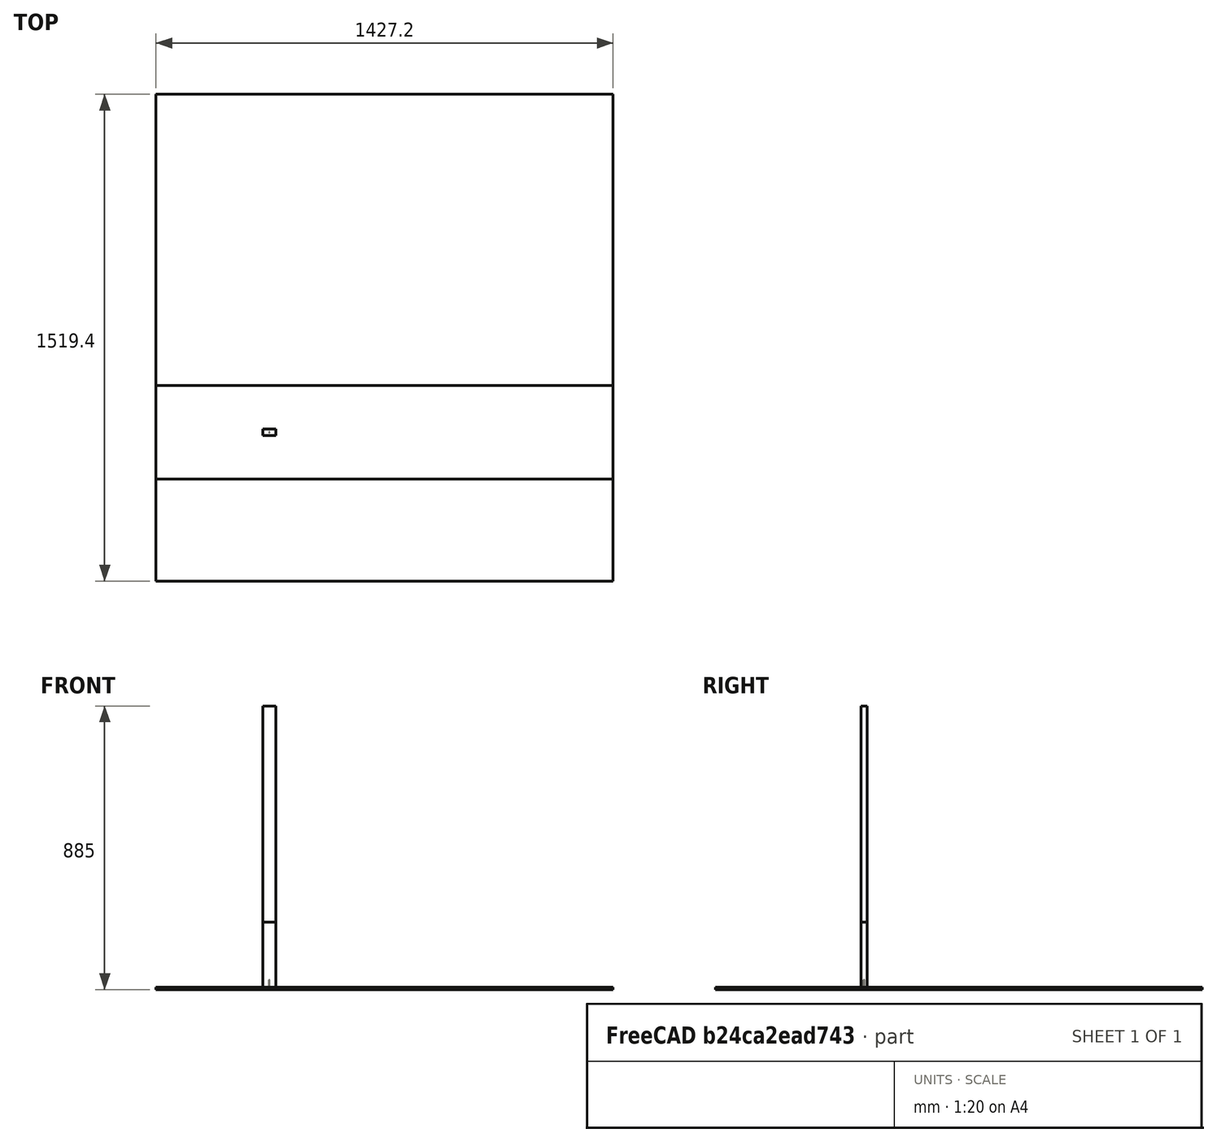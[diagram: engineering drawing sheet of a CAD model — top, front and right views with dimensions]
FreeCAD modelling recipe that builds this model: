
FCSTD DOCUMENT  (FreeCAD 0.22R37100 (Git))
Label: composit_stand10_transport
License: All rights reserved
LicenseURL: http://en.wikipedia.org/wiki/All_rights_reserved
objects: PartDesign::CoordinateSystem×13, App::FeaturePython×13, App::Link×12, Part::FeaturePython×10, App::DocumentObjectGroup×9, Sketcher::SketchObject×8, Path::FeaturePython×7, PartDesign::Pad×5, PartDesign::Body×5, PartDesign::Pocket×3, Measure::MeasureLength×2, Assembly::JointGroup×1, Assembly::AssemblyObject×1
note: 55 computed .brp shape members not serialized (recipe doc carries the construction recipe); baked Part::Feature solids carry a one-line shape summary decoded from their .brp

FEATURE [Sketcher::SketchObject] Sketch  label="front_Sketch"
  AttachmentSupport = -> [XY_Plane]
  FullyConstrained = true
  MapMode = 5
  sketch-geometry (5):
    g0: LineSegment StartX=-355.5 StartY=-465.5 StartZ=0 EndX=355.5 EndY=-465.5 EndZ=0
    g1: LineSegment StartX=355.5 StartY=-465.5 StartZ=0 EndX=355.5 EndY=465.5 EndZ=0
    g2: LineSegment StartX=355.5 StartY=465.5 StartZ=0 EndX=-355.5 EndY=465.5 EndZ=0
    g3: LineSegment StartX=-355.5 StartY=465.5 StartZ=0 EndX=-355.5 EndY=-465.5 EndZ=0
    g4: GeomPoint X=0 Y=0 Z=0
  constraints (12):
    c: Coincident(g0,g1)
    c: Coincident(g1,g2)
    c: Coincident(g2,g3)
    c: Coincident(g3,g0)
    c: Horizontal(g0)
    c: Horizontal(g2)
    c: Vertical(g1)
    c: Vertical(g3)
    c: Symmetric(g2,g0,g4)
    c: Coincident(g4,g-1)
    c: DistanceX(g0,g1) = 711  'width'
    c: DistanceY(g0,g1) = 931  'height'
FEATURE [PartDesign::Pad] Pad
  Direction = (0,0,1)
  Length = 6
  Length2 = 10
  Profile = -> Sketch
  ReferenceAxis = -> Sketch [N_Axis]
  Suppressed = false
  Type = 0
FEATURE [Sketcher::SketchObject] Sketch001  label="bottom_Sketch"
  AttachmentSupport = -> [XY_Plane001]
  FullyConstrained = true
  MapMode = 5
  sketch-geometry (5):
    g0: LineSegment StartX=-355.5 StartY=-145 StartZ=0 EndX=355.5 EndY=-145 EndZ=0
    g1: LineSegment StartX=355.5 StartY=-145 StartZ=0 EndX=355.5 EndY=145 EndZ=0
    g2: LineSegment StartX=355.5 StartY=145 StartZ=0 EndX=-355.5 EndY=145 EndZ=0
    g3: LineSegment StartX=-355.5 StartY=145 StartZ=0 EndX=-355.5 EndY=-145 EndZ=0
    g4: GeomPoint X=0 Y=0 Z=0
  constraints (12):
    c: Coincident(g0,g1)
    c: Coincident(g1,g2)
    c: Coincident(g2,g3)
    c: Coincident(g3,g0)
    c: Horizontal(g0)
    c: Horizontal(g2)
    c: Vertical(g1)
    c: Vertical(g3)
    c: Symmetric(g2,g0,g4)
    c: Coincident(g4,g-1)
    c: DistanceX(g0,g1) = 711  'width'
    c: DistanceY(g0,g1) = 290  'length'
FEATURE [PartDesign::Pad] Pad001
  Direction = (0,0,1)
  Length = 6
  Length2 = 10
  Profile = -> Sketch001
  ReferenceAxis = -> Sketch001 [N_Axis]
  Suppressed = false
  Type = 0
FEATURE [Sketcher::SketchObject] Sketch002  label="side_Sketch"
  AttachmentSupport = -> [XY_Plane002]
  FullyConstrained = true
  MapMode = 5
  sketch-geometry (5):
    g0: LineSegment StartX=-145 StartY=-442.5 StartZ=0 EndX=145 EndY=-442.5 EndZ=0
    g1: LineSegment StartX=145 StartY=-442.5 StartZ=0 EndX=145 EndY=442.5 EndZ=0
    g2: LineSegment StartX=145 StartY=442.5 StartZ=0 EndX=-145 EndY=442.5 EndZ=0
    g3: LineSegment StartX=-145 StartY=442.5 StartZ=0 EndX=-145 EndY=-442.5 EndZ=0
    g4: GeomPoint X=0 Y=0 Z=0
  constraints (12):
    c: Coincident(g0,g1)
    c: Coincident(g1,g2)
    c: Coincident(g2,g3)
    c: Coincident(g3,g0)
    c: Horizontal(g0)
    c: Horizontal(g2)
    c: Vertical(g1)
    c: Vertical(g3)
    c: Symmetric(g2,g0,g4)
    c: Coincident(g4,g-1)
    c: DistanceX(g0,g1) = 290  'length'
    c: DistanceY(g0,g1) = 885  'height'
FEATURE [PartDesign::Pad] Pad002
  Direction = (0,0,1)
  Length = 6
  Length2 = 10
  Profile = -> Sketch002
  ReferenceAxis = -> Sketch002 [N_Axis]
  Suppressed = false
  Type = 0
FEATURE [Sketcher::SketchObject] Sketch003  label="bar_big_Sketch"
  AttachmentSupport = -> [XY_Plane003]
  FullyConstrained = true
  MapMode = 5
  sketch-geometry (5):
    g0: LineSegment StartX=-20 StartY=-10 StartZ=0 EndX=20 EndY=-10 EndZ=0
    g1: LineSegment StartX=20 StartY=-10 StartZ=0 EndX=20 EndY=10 EndZ=0
    g2: LineSegment StartX=20 StartY=10 StartZ=0 EndX=-20 EndY=10 EndZ=0
    g3: LineSegment StartX=-20 StartY=10 StartZ=0 EndX=-20 EndY=-10 EndZ=0
    g4: GeomPoint X=0 Y=0 Z=0
  constraints (12):
    c: Coincident(g0,g1)
    c: Coincident(g1,g2)
    c: Coincident(g2,g3)
    c: Coincident(g3,g0)
    c: Horizontal(g0)
    c: Horizontal(g2)
    c: Vertical(g1)
    c: Vertical(g3)
    c: Symmetric(g2,g0,g4)
    c: Coincident(g4,g-1)
    c: DistanceX(g0,g1) = 40
    c: DistanceY(g0,g1) = 20
FEATURE [PartDesign::Pad] Pad003
  Direction = (0,0,1)
  Length = 885
  Length2 = 10
  Profile = -> Sketch003
  ReferenceAxis = -> Sketch003 [N_Axis]
  Suppressed = false
  Type = 0
FEATURE [Sketcher::SketchObject] Sketch004  label="bar_small_Sketch"
  AttachmentSupport = -> [XY_Plane004]
  FullyConstrained = true
  MapMode = 5
  sketch-geometry (5):
    g0: LineSegment StartX=-20 StartY=-10 StartZ=0 EndX=20 EndY=-10 EndZ=0
    g1: LineSegment StartX=20 StartY=-10 StartZ=0 EndX=20 EndY=10 EndZ=0
    g2: LineSegment StartX=20 StartY=10 StartZ=0 EndX=-20 EndY=10 EndZ=0
    g3: LineSegment StartX=-20 StartY=10 StartZ=0 EndX=-20 EndY=-10 EndZ=0
    g4: GeomPoint X=0 Y=0 Z=0
  constraints (12):
    c: Coincident(g0,g1)
    c: Coincident(g1,g2)
    c: Coincident(g2,g3)
    c: Coincident(g3,g0)
    c: Horizontal(g0)
    c: Horizontal(g2)
    c: Vertical(g1)
    c: Vertical(g3)
    c: Symmetric(g2,g0,g4)
    c: Coincident(g4,g-1)
    c: DistanceX(g0,g1) = 40
    c: DistanceY(g0,g1) = 20
FEATURE [PartDesign::Pad] Pad004
  Direction = (0,0,1)
  Length = 210
  Length2 = 10
  Profile = -> Sketch004
  ReferenceAxis = -> Sketch004 [N_Axis]
  Suppressed = false
  Type = 0
FEATURE [PartDesign::CoordinateSystem] Local_CS  label="front_bottom_LCS"
  AttacherType = Attacher::AttachEngine3D
  AttachmentOffset = pos=(0,-445.5,0) rot=(0,0,1;0rad)
  AttachmentSupport = -> [XY_Plane]
  MapMode = 5
  Placement = pos=(0,-445.5,0) rot=(0,0,1;0rad)
  expr: .AttachmentOffset.Base.y = -<<front_Sketch>>.Constraints.height / 2 + 20 mm
FEATURE [PartDesign::CoordinateSystem] Local_CS001  label="bottom_front_LCS"
  AttacherType = Attacher::AttachEngine3D
  AttachmentOffset = pos=(0,-145,0) rot=(1,0,0;1.5708rad)
  AttachmentSupport = -> [XY_Plane001]
  MapMode = 5
  Placement = pos=(0,-145,0) rot=(1,0,0;1.5708rad)
  expr: .AttachmentOffset.Base.y = -<<bottom_Sketch>>.Constraints.length / 2
FEATURE [PartDesign::CoordinateSystem] Local_CS002  label="bottom_side_LCS"
  AttacherType = Attacher::AttachEngine3D
  AttachmentOffset = pos=(329.5,0,6) rot=(0.57735,0.57735,0.57735;2.0944rad)
  AttachmentSupport = -> [XY_Plane001]
  MapMode = 5
  Placement = pos=(329.5,0,6) rot=(0.57735,0.57735,0.57735;2.0944rad)
  expr: .AttachmentOffset.Base.x = <<bottom_Sketch>>.Constraints.width / 2 - 26 mm
FEATURE [App::FeaturePython] SetupSheet  # Path/CAM operation (typed FeaturePython)
  ClearanceHeightExpression = OpStockZMax+SetupSheet.ClearanceHeightOffset
  ClearanceHeightOffset = 5
  CoolantMode = 0
  CoolantModes = None | Flood | Mist
  FinalDepthExpression = OpFinalDepth
  HorizRapid = 0
  ProfileDirection = 1
  ProfileprocessCircles = true
  ProfileprocessHoles = true
  ProfileprocessPerimeter = true
  SafeHeightExpression = OpStockZMax+SetupSheet.SafeHeightOffset
  SafeHeightOffset = 3
  StartDepthExpression = OpStartDepth
  StepDownExpression = OpToolDiameter
  VertRapid = 0
FEATURE [Part::FeaturePython] ToolBit  label="3.175mm Endmill"  # Path/CAM toolbit (typed FeaturePython)
  BitPropertyNames = Chipload | CuttingEdgeHeight | Diameter | Flutes | Length | Material | ShankDiameter | SpindleDirection
  BitShape = <path>
  Chipload = 0
  CuttingEdgeHeight = 30
  Diameter = 3.17
  Flutes = 0
  Length = 10
  Material = 0
  ShankDiameter = 3
  ShapeName = endmill
  SpindleDirection = 0
FEATURE [Path::FeaturePython] __175mm_Endmill  label="3.175mm Endmill001"  # Path/CAM operation (typed FeaturePython)
  HorizFeed = 51.6667
  HorizRapid = 0
  SpindleDir = 0
  SpindleSpeed = 18000
  Tool = -> ToolBit
  ToolNumber = 1
  VertFeed = 16.6667
  VertRapid = 0
  expr: HorizRapid = SetupSheet.HorizRapid
  expr: VertRapid = SetupSheet.VertRapid
FEATURE [App::DocumentObjectGroup] Tools
  Group = -> [__175mm_Endmill]
FEATURE [App::FeaturePython] SetupSheet001  # Path/CAM operation (typed FeaturePython)
  ClearanceHeightExpression = OpStockZMax+SetupSheet001.ClearanceHeightOffset
  ClearanceHeightOffset = 5
  CoolantMode = 0
  CoolantModes = None | Flood | Mist
  FinalDepthExpression = OpFinalDepth
  HorizRapid = 0
  ProfileDirection = 1
  ProfileprocessCircles = true
  ProfileprocessHoles = true
  ProfileprocessPerimeter = true
  SafeHeightExpression = OpStockZMax+SetupSheet001.SafeHeightOffset
  SafeHeightOffset = 3
  StartDepthExpression = OpStartDepth
  StepDownExpression = OpToolDiameter
  VertRapid = 0
FEATURE [Part::FeaturePython] ToolBit001  label="3.175mm Endmill003"  # Path/CAM toolbit (typed FeaturePython)
  BitPropertyNames = Chipload | CuttingEdgeHeight | Diameter | Flutes | Length | Material | ShankDiameter | SpindleDirection
  BitShape = <path>
  Chipload = 0
  CuttingEdgeHeight = 30
  Diameter = 3.17
  Flutes = 0
  Length = 10
  Material = 0
  ShankDiameter = 3
  ShapeName = endmill
  SpindleDirection = 0
FEATURE [Path::FeaturePython] __175mm_Endmill001  label="3.175mm Endmill002"  # Path/CAM operation (typed FeaturePython)
  HorizFeed = 51.6667
  HorizRapid = 0
  SpindleDir = 0
  SpindleSpeed = 18000
  Tool = -> ToolBit001
  ToolNumber = 1
  VertFeed = 16.6667
  VertRapid = 0
  expr: HorizRapid = SetupSheet001.HorizRapid
  expr: VertRapid = SetupSheet001.VertRapid
FEATURE [App::DocumentObjectGroup] Tools001
  Group = -> [__175mm_Endmill001]
FEATURE [App::Link] bottom  label="bottom001 🔒"
  LinkedObject = -> Body001
FEATURE [App::FeaturePython] GroundedJoint  # Assembly grounded joint (typed FeaturePython)
  ObjectToGround = -> bottom
FEATURE [App::Link] front  label="front001"
  LinkPlacement = pos=(0,-145,445.5) rot=(1,0,0;1.5708rad)
  LinkedObject = -> Body
  Placement = pos=(0,-145,445.5) rot=(1,0,0;1.5708rad)
FEATURE [App::FeaturePython] Fixed  # Assembly joint (typed FeaturePython)
  Activated = true
  Detach1 = false
  Detach2 = false
  Distance = 0
  JointType = 0 (Fixed)
  Object1 = Local_CS
  Object2 = Local_CS001
  Offset = (0,0,0)
  Part1 = -> front
  Part2 = -> bottom
  Rotation = 0
FEATURE [PartDesign::CoordinateSystem] Local_CS003  label="bottom_back_LCS"
  AttacherType = Attacher::AttachEngine3D
  AttachmentOffset = pos=(0,145,0) rot=(0,0.707107,0.707107;3.14159rad)
  AttachmentSupport = -> [XY_Plane001]
  MapMode = 5
  Placement = pos=(0,145,0) rot=(0,0.707107,0.707107;3.14159rad)
  expr: .AttachmentOffset.Base.y = <<bottom_Sketch>>.Constraints.length / 2
FEATURE [PartDesign::CoordinateSystem] Local_CS004  label="bottom_side2_LCS"
  AttacherType = Attacher::AttachEngine3D
  AttachmentOffset = pos=(-329.5,0,6) rot=(0.57735,0.57735,0.57735;2.0944rad)
  AttachmentSupport = -> [XY_Plane001]
  MapMode = 5
  Placement = pos=(-329.5,0,6) rot=(0.57735,0.57735,0.57735;2.0944rad)
  expr: .AttachmentOffset.Base.x = -<<bottom_side_LCS>>.Placement.Base.x
FEATURE [App::Link] front001  label="front002"
  LinkPlacement = pos=(0,145,445.5) rot=(0,0.707107,0.707107;3.14159rad)
  LinkedObject = -> Body
  Placement = pos=(0,145,445.5) rot=(0,0.707107,0.707107;3.14159rad)
FEATURE [App::Link] side  label="side001"
  LinkPlacement = pos=(329.5,-1.965e-13,448.5) rot=(0.57735,0.57735,0.57735;2.0944rad)
  LinkedObject = -> Body002
  Placement = pos=(329.5,-1.965e-13,448.5) rot=(0.57735,0.57735,0.57735;2.0944rad)
FEATURE [App::Link] side001  label="side002"
  LinkPlacement = pos=(-329.5,-1.965e-13,448.5) rot=(0.57735,-0.57735,-0.57735;2.0944rad)
  LinkedObject = -> Body002
  Placement = pos=(-329.5,-1.965e-13,448.5) rot=(0.57735,-0.57735,-0.57735;2.0944rad)
FEATURE [App::Link] bottom001
  LinkPlacement = pos=(376.2,376.2,376.2) rot=(0,0,1;0rad)
  LinkedObject = -> Body001
  Placement = pos=(376.2,376.2,376.2) rot=(0,0,1;0rad)
FEATURE [App::FeaturePython] Fixed001  # Assembly joint (typed FeaturePython)
  Activated = true
  Detach1 = false
  Detach2 = false
  Distance = 0
  JointType = 0 (Fixed)
  Object1 = Local_CS003
  Object2 = Local_CS
  Offset = (0,0,0)
  Part1 = -> bottom
  Part2 = -> front001
  Rotation = 0
FEATURE [PartDesign::CoordinateSystem] Local_CS005  label="side_LCS"
  AttacherType = Attacher::AttachEngine3D
  AttachmentOffset = pos=(0,-442.5,0) rot=(0,0,1;0rad)
  AttachmentSupport = -> [XY_Plane002]
  MapMode = 5
  Placement = pos=(0,-442.5,0) rot=(0,0,1;0rad)
  expr: .AttachmentOffset.Base.y = -<<side_Sketch>>.Constraints.height / 2
FEATURE [App::FeaturePython] Fixed002  # Assembly joint (typed FeaturePython)
  Activated = true
  Detach1 = false
  Detach2 = false
  Distance = 0
  JointType = 0 (Fixed)
  Object1 = Local_CS002
  Object2 = Local_CS005
  Offset = (0,0,0)
  Part1 = -> bottom
  Part2 = -> side
  Rotation = 0
FEATURE [App::FeaturePython] Fixed003  # Assembly joint (typed FeaturePython)
  Activated = true
  Detach1 = false
  Detach2 = false
  Distance = 0
  JointType = 0 (Fixed)
  Object1 = Local_CS004
  Object2 = Local_CS005
  Offset = (0,0,0)
  Part1 = -> bottom
  Part2 = -> side001
  Rotation = 0
FEATURE [PartDesign::CoordinateSystem] Local_CS006  label="bar_big_LCS"
  AttacherType = Attacher::AttachEngine3D
  AttachmentOffset = pos=(-20,10,0) rot=(0,0,1;0rad)
  AttachmentSupport = -> [XY_Plane003]
  MapMode = 5
  Placement = pos=(-20,10,0) rot=(0,0,1;0rad)
FEATURE [PartDesign::Body] Body003  label="bar_big"
  Group = -> [Sketch003,Pad003,Local_CS006]
  Origin = -> Origin003
  Tip = -> Pad003
FEATURE [PartDesign::CoordinateSystem] Local_CS007  label="bottom_bar_big1_LCS"
  AttacherType = Attacher::AttachEngine3D
  AttachmentOffset = pos=(355.5,145,6) rot=(0,0,1;-1.5708rad)
  AttachmentSupport = -> [XY_Plane001]
  MapMode = 5
  Placement = pos=(355.5,145,6) rot=(0,0,1;4.71239rad)
  expr: .AttachmentOffset.Base.x = <<bottom_Sketch>>.Constraints.width / 2
  expr: .AttachmentOffset.Base.y = <<bottom_Sketch>>.Constraints.length / 2
FEATURE [App::Link] bar_big  label="bar_big001"
  LinkPlacement = pos=(345.5,125,6) rot=(0,0,-1;1.5708rad)
  LinkedObject = -> Body003
  Placement = pos=(345.5,125,6) rot=(0,0,-1;1.5708rad)
FEATURE [App::FeaturePython] Fixed004  # Assembly joint (typed FeaturePython)
  Activated = true
  Detach1 = false
  Detach2 = false
  Distance = 0
  JointType = 0 (Fixed)
  Object1 = Local_CS007
  Object2 = Local_CS006
  Offset = (0,0,0)
  Part1 = -> bottom
  Part2 = -> bar_big
  Rotation = 0
FEATURE [PartDesign::CoordinateSystem] Local_CS008  label="bottom_bar_big2_LCS"
  AttacherType = Attacher::AttachEngine3D
  AttachmentOffset = pos=(355.5,-105,6) rot=(0,0,1;-1.5708rad)
  AttachmentSupport = -> [XY_Plane001]
  MapMode = 5
  Placement = pos=(355.5,-105,6) rot=(0,0,1;4.71239rad)
  expr: .AttachmentOffset.Base.x = <<bottom_Sketch>>.Constraints.width / 2
  expr: .AttachmentOffset.Base.y = -<<bottom_Sketch>>.Constraints.length / 2 + 40 mm
FEATURE [PartDesign::CoordinateSystem] Local_CS009  label="bottom_bar_big3_LCS"
  AttacherType = Attacher::AttachEngine3D
  AttachmentOffset = pos=(-335.5,145,6) rot=(0,0,1;-1.5708rad)
  AttachmentSupport = -> [XY_Plane001]
  MapMode = 5
  Placement = pos=(-335.5,145,6) rot=(0,0,1;4.71239rad)
  expr: .AttachmentOffset.Base.x = -<<bottom_Sketch>>.Constraints.width / 2 + 20 mm
  expr: .AttachmentOffset.Base.y = <<bottom_Sketch>>.Constraints.length / 2
FEATURE [PartDesign::CoordinateSystem] Local_CS010  label="bottom_bar_big4_LCS"
  AttacherType = Attacher::AttachEngine3D
  AttachmentOffset = pos=(-355.5,-145,6) rot=(0,0,1;-1.5708rad)
  AttachmentSupport = -> [XY_Plane001]
  MapMode = 5
  Placement = pos=(-355.5,-145,6) rot=(0,0,1;4.71239rad)
  expr: .AttachmentOffset.Base.x = -<<bottom_Sketch>>.Constraints.width / 2
  expr: .AttachmentOffset.Base.y = -<<bottom_Sketch>>.Constraints.length / 2
FEATURE [App::Link] bar_big001  label="bar_big002"
  LinkPlacement = pos=(345.5,-125,6) rot=(0,0,-1;1.5708rad)
  LinkedObject = -> Body003
  Placement = pos=(345.5,-125,6) rot=(0,0,-1;1.5708rad)
FEATURE [App::Link] bar_big002  label="bar_big003"
  LinkPlacement = pos=(-345.5,125,6) rot=(0,0,-1;1.5708rad)
  LinkedObject = -> Body003
  Placement = pos=(-345.5,125,6) rot=(0,0,-1;1.5708rad)
FEATURE [App::Link] bar_big003  label="bar_big004"
  LinkPlacement = pos=(-345.5,-125,6) rot=(0,0,1;1.5708rad)
  LinkedObject = -> Body003
  Placement = pos=(-345.5,-125,6) rot=(0,0,1;1.5708rad)
FEATURE [App::FeaturePython] Fixed005  # Assembly joint (typed FeaturePython)
  Activated = true
  Detach1 = false
  Detach2 = false
  Distance = 0
  JointType = 0 (Fixed)
  Object1 = Local_CS008
  Object2 = Local_CS006
  Offset = (0,0,0)
  Part1 = -> bottom
  Part2 = -> bar_big001
  Rotation = 0
FEATURE [App::FeaturePython] Fixed006  # Assembly joint (typed FeaturePython)
  Activated = true
  Detach1 = false
  Detach2 = false
  Distance = 0
  JointType = 0 (Fixed)
  Object1 = Local_CS009
  Object2 = Local_CS006
  Offset = (0,0,0)
  Part1 = -> bottom
  Part2 = -> bar_big002
  Rotation = 0
FEATURE [App::FeaturePython] Fixed007  # Assembly joint (typed FeaturePython)
  Activated = true
  Detach1 = false
  Detach2 = false
  Distance = 0
  JointType = 0 (Fixed)
  Object1 = Local_CS010
  Object2 = Local_CS006
  Offset = (0,0,0)
  Part1 = -> bottom
  Part2 = -> bar_big003
  Rotation = 0
FEATURE [PartDesign::CoordinateSystem] Local_CS011  label="side_bar_LCS"
  AttacherType = Attacher::AttachEngine3D
  AttachmentOffset = pos=(0,-442.5,6) rot=(0,0,1;0rad)
  AttachmentSupport = -> [XY_Plane002]
  MapMode = 5
  Placement = pos=(0,-442.5,6) rot=(0,0,1;0rad)
  expr: .AttachmentOffset.Base.y = -<<side_Sketch>>.Constraints.height / 2
FEATURE [PartDesign::CoordinateSystem] Local_CS012
  AttacherType = Attacher::AttachEngine3D
  AttachmentOffset = pos=(-20,105,-10) rot=(0.707107,-0.707107,0;3.14159rad)
  AttachmentSupport = -> [XZ_Plane004]
  MapMode = 5
  Placement = pos=(-20,10,105) rot=(0.57735,-0.57735,-0.57735;4.18879rad)
FEATURE [PartDesign::Body] Body004  label="bar_small"
  Group = -> [Sketch004,Pad004,Local_CS012]
  Origin = -> Origin004
  Tip = -> Pad004
FEATURE [App::Link] bar_small  label="bar_small001"
  LinkPlacement = pos=(345.5,105,26) rot=(0.57735,-0.57735,0.57735;2.0944rad)
  LinkedObject = -> Body004
  Placement = pos=(345.5,105,26) rot=(0.57735,-0.57735,0.57735;2.0944rad)
FEATURE [App::Link] bar_small001  label="bar_small002"
  LinkPlacement = pos=(-325.5,-105,-14) rot=(0.57735,-0.57735,-0.57735;4.18879rad)
  LinkedObject = -> Body004
  Placement = pos=(-325.5,-105,-14) rot=(0.57735,-0.57735,-0.57735;4.18879rad)
FEATURE [App::FeaturePython] Fixed008  # Assembly joint (typed FeaturePython)
  Activated = true
  Detach1 = false
  Detach2 = false
  Distance = 0
  JointType = 0 (Fixed)
  Object1 = Local_CS011
  Object2 = Local_CS012
  Offset = (0,0,1)
  Part1 = -> side
  Part2 = -> bar_small
  Rotation = 0
FEATURE [App::FeaturePython] Fixed009  # Assembly joint (typed FeaturePython)
  Activated = true
  Detach1 = false
  Detach2 = false
  Distance = 0
  JointType = 0 (Fixed)
  Object1 = Local_CS011
  Object2 = Local_CS012
  Offset = (0,0,0)
  Part1 = -> side001
  Part2 = -> bar_small001
  Rotation = 0
FEATURE [Assembly::JointGroup] Joints
  Group = -> [GroundedJoint,Fixed,Fixed001,Fixed002,Fixed003,Fixed004,Fixed005,Fixed006,Fixed007,Fixed008,Fixed009]
FEATURE [Assembly::AssemblyObject] Assembly
  Group = -> [Joints,bottom,GroundedJoint,front,Fixed,front001,side,side001,bottom001,Fixed001,Fixed002,Fixed003,bar_big,Fixed004,bar_big001,bar_big002,bar_big003,Fixed005,Fixed006,Fixed007,bar_small,bar_small001,Fixed008,Fixed009]
  Origin = -> Origin005
  Type = Assembly
FEATURE [Sketcher::SketchObject] Sketch005
  AttachmentSupport = -> [XY_Plane]
  FullyConstrained = true
  MapMode = 5
  sketch-geometry (2):
    g0: Circle CenterX=315 CenterY=430 CenterZ=0 NormalX=0 NormalY=0 NormalZ=1 AngleXU=0 Radius=1.7
    g1: Circle CenterX=-315 CenterY=-430 CenterZ=0 NormalX=0 NormalY=0 NormalZ=1 AngleXU=0 Radius=1.7
  constraints (5):
    c: Symmetric(g1,g0,g-1)
    c: Equal(g0,g1)
    c: Diameter(g0) = 3.4
    c: DistanceX(g0) = 315
    c: DistanceY(g0) = 430
FEATURE [PartDesign::Pocket] Pocket
  BaseFeature = -> Pad
  Direction = (0,0,-1)
  Length = 5
  Length2 = 5
  Midplane = true
  Profile = -> Sketch005
  ReferenceAxis = -> Sketch005 [N_Axis]
  Suppressed = false
  Type = 1
FEATURE [PartDesign::Body] Body  label="front"
  Group = -> [Sketch,Pad,Local_CS,Sketch005,Pocket]
  Origin = -> Origin
  Tip = -> Pocket
FEATURE [Part::FeaturePython] Clone  label="Model-front"  # Draft clone (typed FeaturePython)
  AttacherType = Attacher::AttachEngine3D
  Fuse = false
  Objects = -> [Body]
  PathResource = Model
  Placement = pos=(355.5,465.5,0) rot=(0,0,1;0rad)
  Scale = (1,1,1)
FEATURE [Part::FeaturePython] Clone001  label="Model-front001"  # Draft clone (typed FeaturePython)
  AttacherType = Attacher::AttachEngine3D
  Fuse = false
  Objects = -> [Body]
  PathResource = Model
  Placement = pos=(1069.7,465.5,0) rot=(0,0,1;0rad)
  Scale = (1,1,1)
FEATURE [Sketcher::SketchObject] Sketch006
  AttachmentSupport = -> [XY_Plane001]
  FullyConstrained = true
  MapMode = 5
  sketch-geometry (2):
    g0: Circle CenterX=325 CenterY=115 CenterZ=0 NormalX=0 NormalY=0 NormalZ=1 AngleXU=0 Radius=1.7
    g1: Circle CenterX=-325 CenterY=-115 CenterZ=0 NormalX=0 NormalY=0 NormalZ=1 AngleXU=0 Radius=1.7
  constraints (5):
    c: Symmetric(g0,g1,g-1)
    c: DistanceX(g0) = 325
    c: DistanceY(g0) = 115
    c: Equal(g0,g1)
    c: Diameter(g0) = 3.4
FEATURE [PartDesign::Pocket] Pocket001
  BaseFeature = -> Pad001
  Direction = (0,0,-1)
  Length = 5
  Length2 = 5
  Midplane = true
  Profile = -> Sketch006
  ReferenceAxis = -> Sketch006 [N_Axis]
  Suppressed = false
  Type = 1
FEATURE [PartDesign::Body] Body001  label="bottom"
  Group = -> [Sketch001,Pad001,Local_CS001,Local_CS002,Local_CS003,Local_CS004,Local_CS007,Local_CS008,Local_CS009,Local_CS010,Sketch006,Pocket001]
  Origin = -> Origin001
  Tip = -> Pocket001
FEATURE [Part::FeaturePython] Clone004  label="Model-bottom"  # Draft clone (typed FeaturePython)
  AttacherType = Attacher::AttachEngine3D
  Fuse = false
  Objects = -> [Body001]
  PathResource = Model
  Placement = pos=(355.5,145,0) rot=(0,0,1;0rad)
  Scale = (1,1,1)
FEATURE [Part::FeaturePython] Clone005  label="Model-bottom001"  # Draft clone (typed FeaturePython)
  AttacherType = Attacher::AttachEngine3D
  Fuse = false
  Objects = -> [Body001]
  PathResource = Model
  Placement = pos=(1069.7,145,0) rot=(0,0,1;0rad)
  Scale = (1,1,1)
FEATURE [App::DocumentObjectGroup] Model001
  Group = -> [Clone004,Clone005]
FEATURE [Part::FeaturePython] Stock001  # WARN: FeaturePython — macro-defined, semantics opaque (R4)
  Base = -> Model001
  ExtXneg = 1
  ExtXpos = 1
  ExtYneg = 1
  ExtYpos = 1
  ExtZneg = 0
  ExtZpos = 1
  Placement = pos=(-353,-145,0) rot=(0,0,1;0rad)
  StockType = FromBase
FEATURE [Path::FeaturePython] Profile001  # Path/CAM operation (typed FeaturePython)
  Active = true
  AreaParams:
    Tolerance = 1e-07
    FitArcs = True
    Simplify = False
    CleanDistance = 0.0
    Accuracy = 0.01
    Unit = 1.0
    MinArcPoints = 4
    MaxArcPoints = 100
    ClipperScale = 10000000.0
    Fill = 0
    Coplanar = 0
    Reorient = True
    Outline = False
    Explode = False
    OpenMode = 0
    Deflection = 0.01
    SubjectFill = 0
    ClipFill = 0
    Offset = 1.585
    ExtraPass = 0
    Stepover = 0.0
    LastStepover = 0.0
    JoinType = 0
    EndType = 0
    MiterLimit = 2.0
    RoundPrecision = 0.0
    PocketMode = 0
    ToolRadius = 1.0
    PocketExtraOffset = 0.0
    PocketStepover = 0.0
    PocketLastStepover = 0.0
    FromCenter = False
    Angle = 45.0
    AngleShift = 0.0
    Shift = 0.0
    Thicken = False
    SectionCount = -1
    Stepdown = 1.0
    SectionOffset = 0.0
    SectionTolerance = 1e-06
    SectionMode = 2
    Project = False
  Base = -> [Clone004,Clone005]
  ClearanceHeight = 12
  CoolantMode = 0
  CycleTime = 00:01:56
  Direction = 1
  FinalDepth = 6
  HandleMultipleFeatures = 0
  JoinType = 0
  MiterLimit = 0.1
  OffsetExtra = 0
  OpFinalDepth = 6
  OpStartDepth = 7
  OpStockZMax = 7
  OpStockZMin = 0
  OpToolDiameter = 3.17
  PathParams = {'orientation': 0, 'feedrate': 51.666666666666664, 'feedrate_v': 16.666666666666668, 'verbose': True, 'resume_height': 10.0, 'retraction': 12.0, 'return_end': True, 'preamble': False, 'start': Vector (1394.5998121756393, 259.9645661900865, 12.0)}
  SafeHeight = 10
  Side = 0
  SplitArcs = false
  StartDepth = 7
  StartPoint = (0,0,0)
  StepDown = 10
  ToolController = -> __175mm_Endmill001
  UseComp = true
  UseStartPoint = false
  processCircles = true
  processHoles = true
  processPerimeter = true
  expr: ClearanceHeight = OpStockZMax + SetupSheet001.ClearanceHeightOffset
  expr: FinalDepth = OpFinalDepth
  expr: SafeHeight = OpStockZMax + SetupSheet001.SafeHeightOffset
  expr: StartDepth = OpStartDepth
FEATURE [App::DocumentObjectGroup] Operations001
  Group = -> [Profile001]
FEATURE [Path::FeaturePython] Job001  label="trans2"  # Path/CAM operation (typed FeaturePython)
  CycleTime = 00:01:56
  Fixtures = G54
  GeometryTolerance = 0.01
  JobType = 0
  LastPostProcessDate = 2024-07-31 15:01:14.415365
  LastPostProcessOutput = <path>
  Model = -> Model001
  Operations = -> Operations001
  OrderOutputBy = 0
  PostProcessor = 13
  PostProcessorOutputFile = <path>
  SetupSheet = -> SetupSheet001
  SplitOutput = false
  Stock = -> Stock001
  Tools = -> Tools001
FEATURE [Sketcher::SketchObject] Sketch007
  AttachmentSupport = -> [XY_Plane002]
  FullyConstrained = true
  MapMode = 5
  sketch-geometry (2):
    g0: Circle CenterX=130 CenterY=425 CenterZ=0 NormalX=0 NormalY=0 NormalZ=1 AngleXU=0 Radius=1.7
    g1: Circle CenterX=-130 CenterY=-425 CenterZ=0 NormalX=0 NormalY=0 NormalZ=1 AngleXU=0 Radius=1.7
  constraints (5):
    c: Symmetric(g0,g1,g-1)
    c: Equal(g0,g1)
    c: Diameter(g0) = 3.4
    c: DistanceX(g0) = 130
    c: DistanceY(g0) = 425
FEATURE [PartDesign::Pocket] Pocket002
  BaseFeature = -> Pad002
  Direction = (0,0,-1)
  Length = 5
  Length2 = 5
  Midplane = true
  Profile = -> Sketch007
  ReferenceAxis = -> Sketch007 [N_Axis]
  Suppressed = false
  Type = 1
FEATURE [PartDesign::Body] Body002  label="side"
  Group = -> [Sketch002,Pad002,Local_CS005,Local_CS011,Sketch007,Pocket002]
  Origin = -> Origin002
  Tip = -> Pocket002
FEATURE [Part::FeaturePython] Clone002  label="Model-side"  # Draft clone (typed FeaturePython)
  AttacherType = Attacher::AttachEngine3D
  Fuse = false
  Objects = -> [Body002]
  PathResource = Model
  Placement = pos=(442.5,1079.2,0) rot=(0,0,1;1.5708rad)
  Scale = (1,1,1)
FEATURE [Part::FeaturePython] Clone003  label="Model-side001"  # Draft clone (typed FeaturePython)
  AttacherType = Attacher::AttachEngine3D
  Fuse = false
  Objects = -> [Body002]
  PathResource = Model
  Placement = pos=(442.5,1372.4,0) rot=(0,0,1;1.5708rad)
  Scale = (1,1,1)
FEATURE [App::DocumentObjectGroup] Model
  Group = -> [Clone,Clone001,Clone002,Clone003]
FEATURE [Part::FeaturePython] Stock  # WARN: FeaturePython — macro-defined, semantics opaque (R4)
  Base = -> Model
  ExtXneg = 1
  ExtXpos = 1
  ExtYneg = 1
  ExtYpos = 1
  ExtZneg = 0
  ExtZpos = 1
  Placement = pos=(-353,-463,0) rot=(0,0,1;0rad)
  StockType = FromBase
FEATURE [App::DocumentObjectGroup] Group  label="parts"
  Group = -> [Body,Body001,Body002,Body003,Body004]
FEATURE [Path::FeaturePython] Profile  # Path/CAM operation (typed FeaturePython)
  Active = true
  AreaParams:
    Tolerance = 1e-07
    FitArcs = True
    Simplify = False
    CleanDistance = 0.0
    Accuracy = 0.01
    Unit = 1.0
    MinArcPoints = 4
    MaxArcPoints = 100
    ClipperScale = 10000000.0
    Fill = 0
    Coplanar = 0
    Reorient = True
    Outline = False
    Explode = False
    OpenMode = 0
    Deflection = 0.01
    SubjectFill = 0
    ClipFill = 0
    Offset = -1.585
    ExtraPass = 0
    Stepover = 0.0
    LastStepover = 0.0
    JoinType = 0
    EndType = 0
    MiterLimit = 2.0
    RoundPrecision = 0.0
    PocketMode = 0
    ToolRadius = 1.0
    PocketExtraOffset = 0.0
    PocketStepover = 0.0
    PocketLastStepover = 0.0
    FromCenter = False
    Angle = 45.0
    AngleShift = 0.0
    Shift = 0.0
    Thicken = False
    SectionCount = -1
    Stepdown = 1.0
    SectionOffset = 0.0
    SectionTolerance = 1e-06
    SectionMode = 2
    Project = False
  Base = -> [Clone001,Clone,Clone002,Clone003]
  ClearanceHeight = 25
  CoolantMode = 0
  CycleTime = 00:01:51
  Direction = 1
  FinalDepth = 0
  HandleMultipleFeatures = 0
  JoinType = 0
  MiterLimit = 0.1
  OffsetExtra = 0
  OpFinalDepth = 0
  OpStartDepth = 7
  OpStockZMax = 7
  OpStockZMin = 0
  OpToolDiameter = 3.17
  PathParams = {'orientation': 1, 'feedrate': 51.666666666666664, 'feedrate_v': 16.666666666666668, 'verbose': True, 'resume_height': 10.0, 'retraction': 25.0, 'return_end': True, 'preamble': False, 'start': Vector (17.603578392297713, 1209.1762371899313, 25.0)}
  SafeHeight = 10
  Side = 0
  SplitArcs = false
  StartDepth = 7
  StartPoint = (0,0,0)
  StepDown = 10
  ToolController = -> __175mm_Endmill
  UseComp = true
  UseStartPoint = false
  processCircles = true
  processHoles = true
  processPerimeter = false
  expr: FinalDepth = OpFinalDepth
  expr: SafeHeight = OpStockZMax + SetupSheet.SafeHeightOffset
  expr: StartDepth = OpStartDepth
FEATURE [Path::FeaturePython] Profile002  # Path/CAM operation (typed FeaturePython)
  Active = true
  AreaParams:
    Tolerance = 1e-07
    FitArcs = True
    Simplify = False
    CleanDistance = 0.0
    Accuracy = 0.01
    Unit = 1.0
    MinArcPoints = 4
    MaxArcPoints = 100
    ClipperScale = 10000000.0
    Fill = 0
    Coplanar = 0
    Reorient = True
    Outline = False
    Explode = False
    OpenMode = 0
    Deflection = 0.01
    SubjectFill = 0
    ClipFill = 0
    Offset = 1.585
    ExtraPass = 0
    Stepover = 0.0
    LastStepover = 0.0
    JoinType = 0
    EndType = 0
    MiterLimit = 2.0
    RoundPrecision = 0.0
    PocketMode = 0
    ToolRadius = 1.0
    PocketExtraOffset = 0.0
    PocketStepover = 0.0
    PocketLastStepover = 0.0
    FromCenter = False
    Angle = 45.0
    AngleShift = 0.0
    Shift = 0.0
    Thicken = False
    SectionCount = -1
    Stepdown = 1.0
    SectionOffset = 0.0
    SectionTolerance = 1e-06
    SectionMode = 2
    Project = False
  Base = -> [Clone001,Clone,Clone002,Clone003]
  ClearanceHeight = 25
  CoolantMode = 0
  CycleTime = 00:04:26
  Direction = 1
  FinalDepth = 0
  HandleMultipleFeatures = 0
  JoinType = 0
  MiterLimit = 0.1
  OffsetExtra = 0
  OpFinalDepth = 0
  OpStartDepth = 7
  OpStockZMax = 7
  OpStockZMin = 0
  OpToolDiameter = 3.17
  PathParams = {'orientation': 0, 'feedrate': 51.666666666666664, 'feedrate_v': 16.666666666666668, 'verbose': True, 'resume_height': 10.0, 'retraction': 25.0, 'return_end': True, 'preamble': False, 'start': Vector (712.1207642321503, 1225.8150000500002, 25.0)}
  SafeHeight = 10
  Side = 0
  SplitArcs = false
  StartDepth = 7
  StartPoint = (0,0,0)
  StepDown = 10
  ToolController = -> __175mm_Endmill
  UseComp = true
  UseStartPoint = false
  processCircles = false
  processHoles = false
  processPerimeter = true
  expr: Base = <<Profile>>.Base
  expr: FinalDepth = OpFinalDepth
  expr: SafeHeight = OpStockZMax + SetupSheet.SafeHeightOffset
  expr: StartDepth = OpStartDepth
FEATURE [App::DocumentObjectGroup] Operations
  Group = -> [Profile,Profile002]
FEATURE [Path::FeaturePython] Job  label="trans"  # Path/CAM operation (typed FeaturePython)
  CycleTime = 00:06:17
  Fixtures = G54
  GeometryTolerance = 0.01
  JobType = 0
  LastPostProcessDate = 2024-07-31 15:28:32.854295
  LastPostProcessOutput = <path> \n/mnt/flash/table/transport/1-1-10_trans-1.tap
  Model = -> Model
  Operations = -> Operations
  OrderOutputBy = 2
  PostProcessor = 13
  PostProcessorOutputFile = <path>
  SetupSheet = -> SetupSheet
  SplitOutput = true
  Stock = -> Stock
  Tools = -> Tools
FEATURE [App::DocumentObjectGroup] Group001  label="jobs"
  Group = -> [Job,Job001]
FEATURE [Measure::MeasureLength] Length
  Elements = -> [Clone004]
  Length = 290
FEATURE [App::DocumentObjectGroup] Measurements
  Group = -> [Length]
FEATURE [Measure::MeasureLength] Length001
  Elements = -> [Clone004]
  Length = 711
note: 6 file-system paths scrubbed to <path> (originals preserved in the JSON sidecar)
